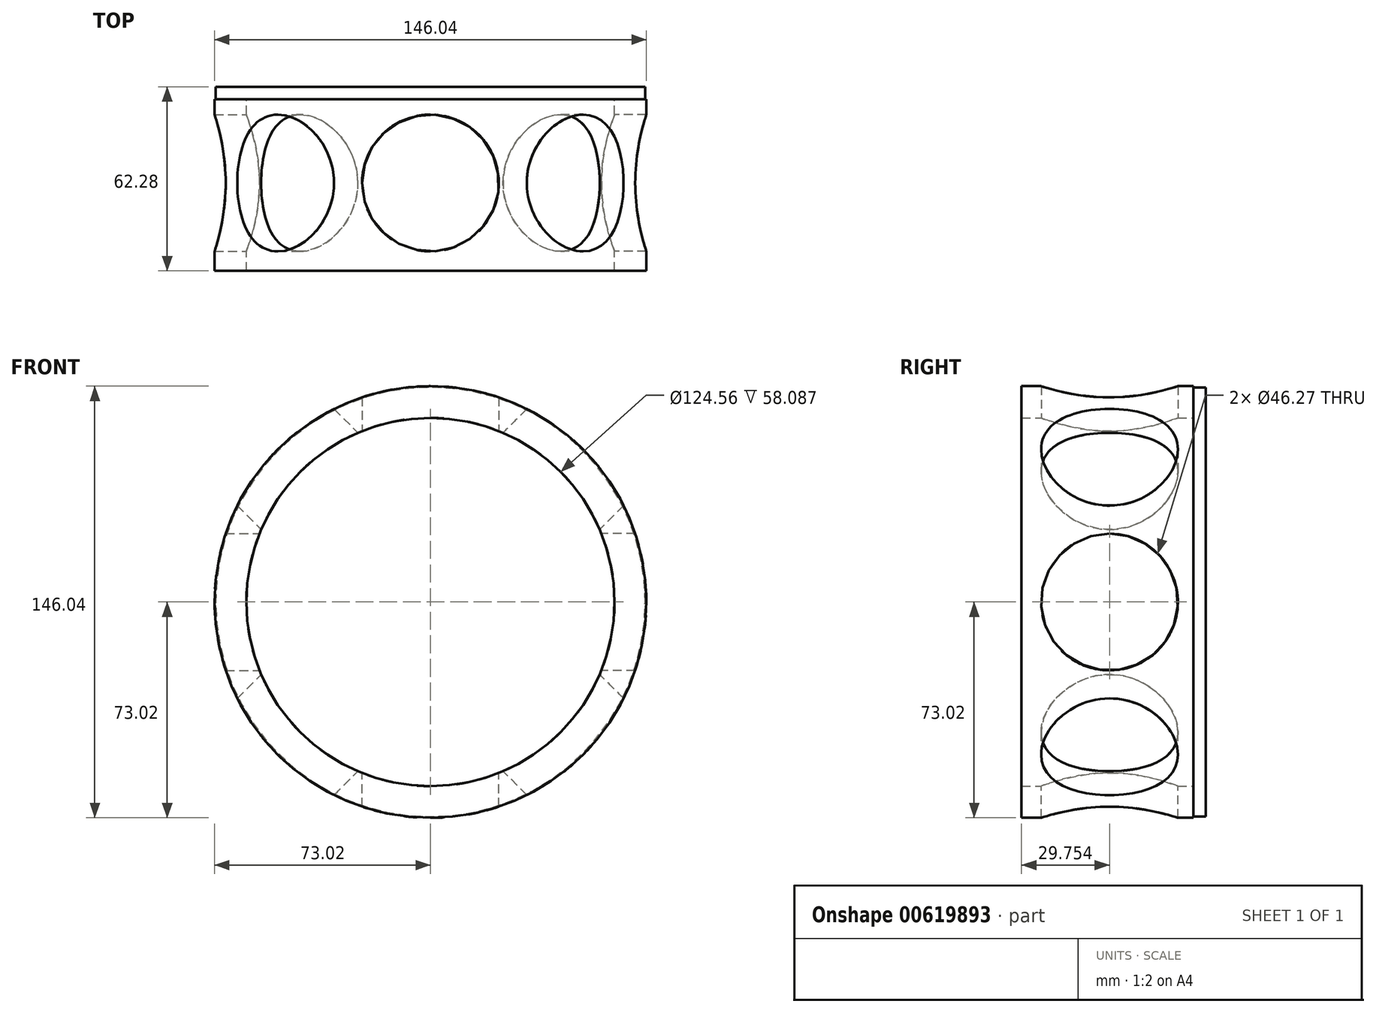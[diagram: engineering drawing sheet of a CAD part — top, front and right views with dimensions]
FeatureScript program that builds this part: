
annotation { "Feature Type Name" : "Feature", "Feature Type Description" : "" }
export const myFeature = defineFeature(function(context is Context, id is Id, definition is map)
    precondition{}
    {
        {
            var Q0;
            Q0=qCreatedBy(makeId("Front.planeOp"),FACE);
            var sketch = newSketch(context, id + "F0", { "sketchPlane" : qUnion([Q0])});
            skCircle(sketch, "E0", {"center": v(0, 0) * mm, "radius": 62.28 * mm});
            skCircle(sketch, "E1", {"center": v(0, 0) * mm, "radius": 73.02 * mm});
            skSolve(sketch);
        }
        {
            var Q0;
            Q0 = qSketchRegion(id + "F0", true);
            extrude(context, id + "F1", {"entities" : qUnion([Q0]), "depth" : 58.1 * mm, "offsetDistance" : 25.4 * mm});
        }
        {
            var Q0;
            Q0=qCreatedBy(makeId("Front.planeOp"),FACE);
            var sketch = newSketch(context, id + "F2", { "sketchPlane" : qUnion([Q0])});
            skCircle(sketch, "E2", {"center": v(0, 0) * mm, "radius": 72.61 * mm});
            skSolve(sketch);
        }
        {
            var Q0;
            Q0 = qSketchRegion(id + "F2", true);
            extrude(context, id + "F3", {"entities" : qUnion([Q0]), "operationType" : NewBodyOperationType.ADD, "oppositeDirection" : true, "depth" : 4.2 * mm, "offsetDistance" : 25.4 * mm});
        }
        {
            var Q0;
            Q0=qCreatedBy(makeId("Right.planeOp"),FACE);
            var sketch = newSketch(context, id + "F4", { "sketchPlane" : qUnion([Q0])});
            skCircle(sketch, "E3", {"center": v(-28.34, 0) * mm, "radius": 23.13 * mm});
            skSolve(sketch);
        }
        {
            var Q0;
            Q0 = qSketchRegion(id + "F4", true);
            extrude(context, id + "F5", {"entities" : qUnion([Q0]), "operationType" : NewBodyOperationType.REMOVE, "oppositeDirection" : true, "depth" : 203.13 * mm, "offsetDistance" : 25.4 * mm});
        }
        {
            var Q0;
            Q0=makeQuery(id+"F5.boolean.opBoolean","COPY",FACE,{"derivedFrom":makeQuery(id+"F5.opExtrude","SWEPT_FACE",FACE,{"disambiguationData":[OSD([sQuery(id+"F4.wireOp",EDGE,"E3")])]})});
            var Q1;
            Q1=makeQuery(id+"F1.opExtrude","CAP_EDGE",EDGE,{"disambiguationData":[OSD([sQuery(id+"F0.wireOp",EDGE,"E0")])],"isStart":false});
            circularPattern(context, id + "F6", {"patternType" : PatternType.FACE, "faces" : qUnion([Q0]), "axis" : qUnion([Q1]), "angle" : 360 * degree, "instanceCount" : 8, "equalSpace" : true});
        }
    });
